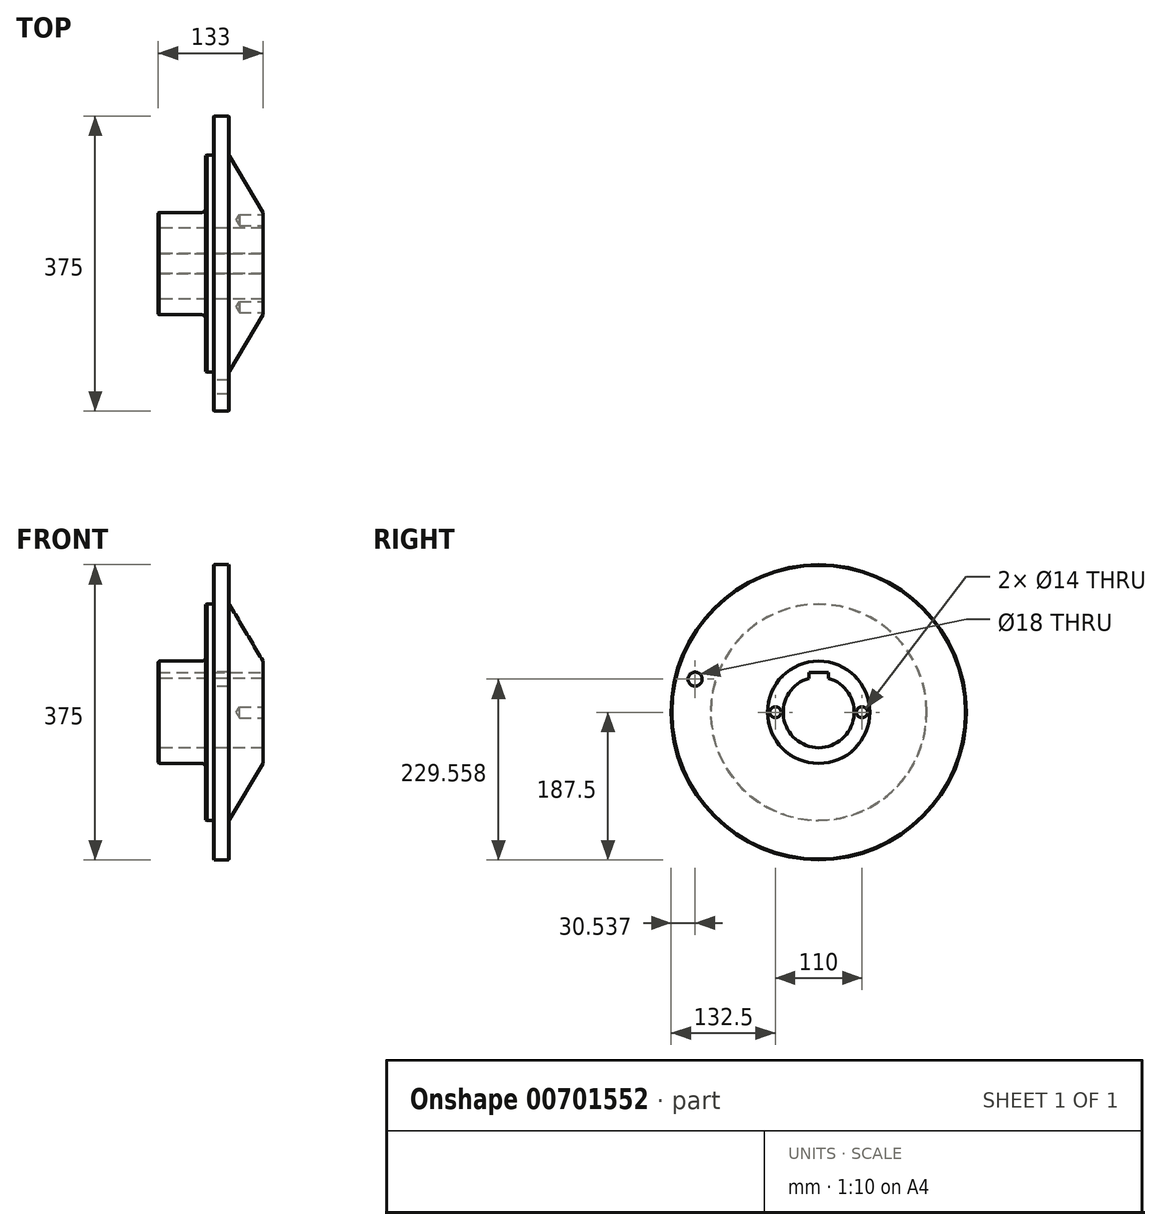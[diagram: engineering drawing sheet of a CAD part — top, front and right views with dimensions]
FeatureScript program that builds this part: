
annotation { "Feature Type Name" : "Feature", "Feature Type Description" : "" }
export const myFeature = defineFeature(function(context is Context, id is Id, definition is map)
    precondition{}
    {
        {
            var Q0;
            Q0=qCreatedBy(makeId("Front.planeOp"),FACE);
            var sketch = newSketch(context, id + "F0", { "sketchPlane" : qUnion([Q0])});
            skLineSegment(sketch, "E0", {"start": v(0, 0) * mm, "end": v(175.43, 0) * mm, "construction": true});
            skLineSegment(sketch, "E1", {"start": v(0, 45) * mm, "end": v(0, 65) * mm});
            skLineSegment(sketch, "E2", {"start": v(0, 65) * mm, "end": v(60, 65) * mm});
            skLineSegment(sketch, "E3", {"start": v(60, 65) * mm, "end": v(60, 137.5) * mm});
            skLineSegment(sketch, "E4", {"start": v(60, 137.5) * mm, "end": v(70, 137.5) * mm});
            skLineSegment(sketch, "E5", {"start": v(70, 137.5) * mm, "end": v(70, 187.5) * mm});
            skLineSegment(sketch, "E6", {"start": v(70, 187.5) * mm, "end": v(90, 187.5) * mm});
            skLineSegment(sketch, "E7", {"start": v(90, 187.5) * mm, "end": v(90, 137.5) * mm});
            skLineSegment(sketch, "E8", {"start": v(90, 137.5) * mm, "end": v(133, 65) * mm});
            skLineSegment(sketch, "E9", {"start": v(133, 65) * mm, "end": v(133, 45) * mm});
            skLineSegment(sketch, "E10", {"start": v(133, 45) * mm, "end": v(0, 45) * mm});
            skSolve(sketch);
        }
        {
            var Q0;
            Q0=makeQuery(id+"F0.imprint","IMPRINT",FACE,{"disambiguationData":[TD([[makeQuery(id+"F0.imprint","IMPRINT",EDGE,{"derivedFrom":sQuery(id+"F0.wireOp",EDGE,"E1")}),-1.0]])]});
            var Q1;
            Q1=sQuery(id+"F0.wireOp",EDGE,"E0");
            revolve(context, id + "F1", {"entities" : qUnion([Q0]), "axis" : qUnion([Q1]), "revolveType" : RevolveType.FULL});
        }
        {
            var Q0;
            Q0=makeQuery(id+"F1.opRevolve","SWEPT_EDGE",EDGE,{"disambiguationData":[OSD([sQuery(id+"F0.wireOp",EDGE,"E3"),sQuery(id+"F0.wireOp",EDGE,"E4")])]});
            chamfer(context, id + "F2", {"entities" : qUnion([Q0]), "chamferType" : ChamferType.OFFSET_ANGLE, "width" : 2 * mm, "oppositeDirection" : true, "angle" : 15 * degree, "tangentPropagation" : true});
        }
        {
            var Q0;
            Q0=makeQuery(id+"F1.opRevolve","SWEPT_EDGE",EDGE,{"disambiguationData":[OSD([sQuery(id+"F0.wireOp",EDGE,"E2"),sQuery(id+"F0.wireOp",EDGE,"E3")])]});
            var Q1;
            Q1=makeQuery(id+"F1.opRevolve","SWEPT_EDGE",EDGE,{"disambiguationData":[OSD([sQuery(id+"F0.wireOp",EDGE,"E7"),sQuery(id+"F0.wireOp",EDGE,"E8")])]});
            fillet(context, id + "F3", {"entities" : qUnion([Q0, Q1]), "radius" : 5 * mm, "tangentPropagation" : true, "allowEdgeOverflow" : false});
        }
        {
            var Q0;
            Q0=makeQuery(id+"F1.opRevolve","SWEPT_EDGE",EDGE,{"disambiguationData":[OSD([sQuery(id+"F0.wireOp",EDGE,"E1"),sQuery(id+"F0.wireOp",EDGE,"E2")])]});
            var Q1;
            Q1=makeQuery(id+"F1.opRevolve","SWEPT_EDGE",EDGE,{"disambiguationData":[OSD([sQuery(id+"F0.wireOp",EDGE,"E5"),sQuery(id+"F0.wireOp",EDGE,"E6")])]});
            var Q2;
            Q2=makeQuery(id+"F1.opRevolve","SWEPT_EDGE",EDGE,{"disambiguationData":[OSD([sQuery(id+"F0.wireOp",EDGE,"E6"),sQuery(id+"F0.wireOp",EDGE,"E7")])]});
            chamfer(context, id + "F4", {"entities" : qUnion([Q0, Q1, Q2]), "width" : 1 * mm, "tangentPropagation" : true});
        }
        {
            var Q0;
            Q0=makeQuery(id+"F1.opRevolve","SWEPT_EDGE",EDGE,{"disambiguationData":[OSD([sQuery(id+"F0.wireOp",EDGE,"E4"),sQuery(id+"F0.wireOp",EDGE,"E5")])]});
            fillet(context, id + "F5", {"entities" : qUnion([Q0]), "radius" : 2 * mm, "tangentPropagation" : true, "allowEdgeOverflow" : false});
        }
        {
            var Q0;
            Q0=makeQuery(id+"F1.opRevolve","SWEPT_EDGE",EDGE,{"disambiguationData":[OSD([sQuery(id+"F0.wireOp",EDGE,"E1"),sQuery(id+"F0.wireOp",EDGE,"E10")])]});
            fillet(context, id + "F6", {"entities" : qUnion([Q0]), "radius" : 3 * mm, "allowEdgeOverflow" : false});
        }
        {
            var Q0;
            Q0=makeQuery(id+"F1.opRevolve","SWEPT_FACE",FACE,{"disambiguationData":[OSD([sQuery(id+"F0.wireOp",EDGE,"E9")])]});
            var sketch = newSketch(context, id + "F7", { "sketchPlane" : qUnion([Q0])});
            skPoint(sketch, "E11", {"position": v(55, 0) * mm});
            skPoint(sketch, "E12", {"position": v(-55, 0) * mm});
            skCircle(sketch, "E13", {"center": v(0, 0) * mm, "radius": 55 * mm, "construction": true});
            skSolve(sketch);
        }
        {
            var Q0;
            Q0=sQuery(id+"F7.wireOp",VERTEX,"E11");
            var Q1;
            Q1=sQuery(id+"F7.wireOp",VERTEX,"E12");
            var Q2;
            Q2=makeQuery(id+"F1.opRevolve","SWEPT_BODY",BODY,{"disambiguationData":[OSD([sQuery(id+"F0.wireOp",EDGE,"E1"),sQuery(id+"F0.wireOp",EDGE,"E2"),sQuery(id+"F0.wireOp",EDGE,"E3"),sQuery(id+"F0.wireOp",EDGE,"E4"),sQuery(id+"F0.wireOp",EDGE,"E5"),sQuery(id+"F0.wireOp",EDGE,"E6"),sQuery(id+"F0.wireOp",EDGE,"E7"),sQuery(id+"F0.wireOp",EDGE,"E8"),sQuery(id+"F0.wireOp",EDGE,"E9"),sQuery(id+"F0.wireOp",EDGE,"E10")])]});
            hole(context, id + "F8", {"style" : HoleStyle.SIMPLE, "endStyle" : HoleEndStyle.BLIND, "standardTappedOrClearance" : lookupTablePath({ "standard" : "ISO", "engagement" : "75%", "pitch" : "2 mm", "size" : "M16", "type" : "Tapped" }), "standardBlindInLast" : lookupTablePath({ "standard" : "ISO", "engagement" : "75%", "pitch" : "2 mm", "size" : "M16", "type" : "Tapped" }), "holeDiameter" : 14 * mm, "majorDiameter" : 16 * mm, "showTappedDepth" : true, "holeDepth" : 30 * mm, "isTappedThrough" : true, "tappedDepth" : 24 * mm, "tapClearance" : 3, "locations" : qUnion([Q0, Q1]), "scope" : qUnion([Q2])});
        }
        {
            var Q0;
            Q0=makeQuery(id+"F1.opRevolve","SWEPT_FACE",FACE,{"disambiguationData":[OSD([sQuery(id+"F0.wireOp",EDGE,"E9")])]});
            var sketch = newSketch(context, id + "F9", { "sketchPlane" : qUnion([Q0])});
            skLineSegment(sketch, "E14.bottom", {"start": v(12.5, 36.4) * mm, "end": v(-12.5, 36.4) * mm});
            skLineSegment(sketch, "E14.top", {"start": v(12.5, 50.4) * mm, "end": v(-12.5, 50.4) * mm});
            skLineSegment(sketch, "E14.left", {"start": v(12.5, 36.4) * mm, "end": v(12.5, 50.4) * mm});
            skLineSegment(sketch, "E14.right", {"start": v(-12.5, 36.4) * mm, "end": v(-12.5, 50.4) * mm});
            skPoint(sketch, "E14.middle", {"position": v(0, 43.4) * mm});
            skSolve(sketch);
        }
        {
            var Q0;
            Q0 = qSketchRegion(id + "F9", true);
            extrude(context, id + "F10", {"entities" : qUnion([Q0]), "operationType" : NewBodyOperationType.REMOVE, "endBound" : BoundingType.THROUGH_ALL, "oppositeDirection" : true, "depth" : 25 * mm, "offsetDistance" : 25 * mm});
        }
        {
            var Q0;
            Q0=makeQuery(id+"F1.opRevolve","SWEPT_FACE",FACE,{"disambiguationData":[OSD([sQuery(id+"F0.wireOp",EDGE,"E5")])]});
            var sketch = newSketch(context, id + "F11", { "sketchPlane" : qUnion([Q0])});
            skLineSegment(sketch, "E15", {"start": v(156.96, 42.06) * mm, "end": v(0, 0) * mm, "construction": true});
            skLineSegment(sketch, "E16", {"start": v(0, 0) * mm, "end": v(155.71, 0) * mm, "construction": true});
            skCircle(sketch, "E17", {"center": v(156.96, 42.06) * mm, "radius": 9 * mm});
            skPoint(sketch, "E18.center", {"position": v(0, 0) * mm});
            skSolve(sketch);
        }
        {
            var Q0;
            Q0=makeQuery(id+"F11.imprint","IMPRINT",FACE,{"disambiguationData":[TD([[makeQuery(id+"F11.imprint","IMPRINT",EDGE,{"derivedFrom":sQuery(id+"F11.wireOp",EDGE,"E17")}),1.0]])]});
            extrude(context, id + "F12", {"entities" : qUnion([Q0]), "operationType" : NewBodyOperationType.REMOVE, "oppositeDirection" : true, "depth" : 25 * mm, "offsetDistance" : 25 * mm});
        }
    });
